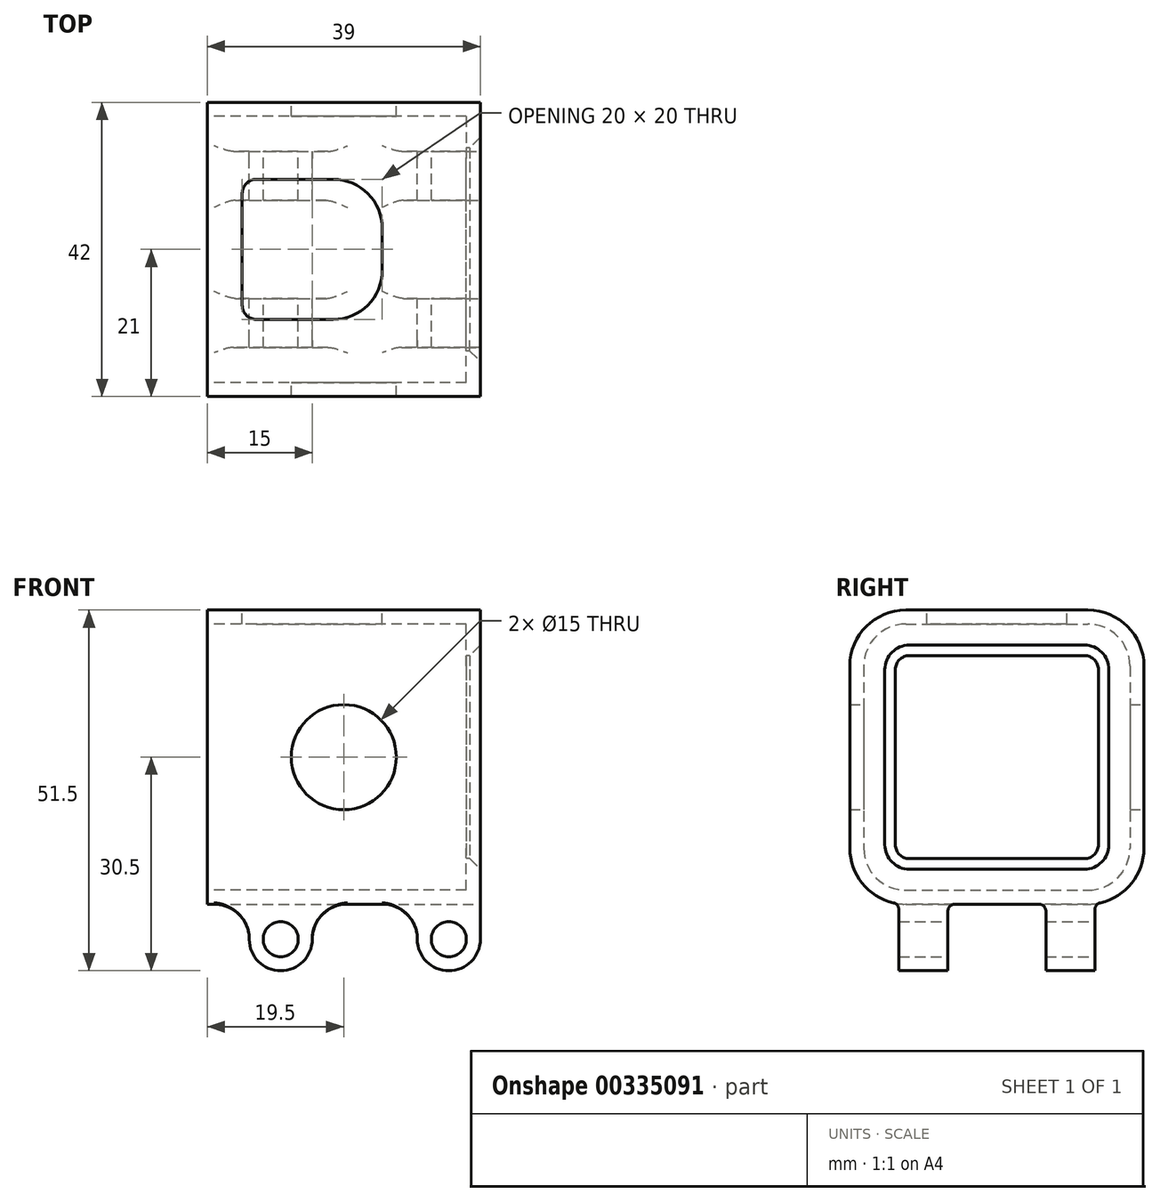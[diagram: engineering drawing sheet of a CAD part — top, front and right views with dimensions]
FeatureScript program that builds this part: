
annotation { "Feature Type Name" : "Feature", "Feature Type Description" : "" }
export const myFeature = defineFeature(function(context is Context, id is Id, definition is map)
    precondition{}
    {
        {
            var Q0;
            Q0=qCreatedBy(makeId("Right.planeOp"),FACE);
            var sketch = newSketch(context, id + "F0", { "sketchPlane" : qUnion([Q0])});
            skLineSegment(sketch, "E0.bottom", {"start": v(-13, 21) * mm, "end": v(13, 21) * mm});
            skLineSegment(sketch, "E0.top", {"start": v(-13, -21) * mm, "end": v(13, -21) * mm});
            skLineSegment(sketch, "E0.left", {"start": v(-21, 13) * mm, "end": v(-21, -13) * mm});
            skLineSegment(sketch, "E0.right", {"start": v(21, 13) * mm, "end": v(21, -13) * mm});
            skLineSegment(sketch, "E1.bottom", {"start": v(-13, 19) * mm, "end": v(13, 19) * mm});
            skLineSegment(sketch, "E1.top", {"start": v(-13, -19) * mm, "end": v(13, -19) * mm});
            skLineSegment(sketch, "E1.left", {"start": v(-19, 13) * mm, "end": v(-19, -13) * mm});
            skLineSegment(sketch, "E1.right", {"start": v(19, 13) * mm, "end": v(19, -13) * mm});
            skPoint(sketch, "E2.visualSharp", {"position": v(-19, 19) * mm});
            skArc(sketch, "E2.filletArc", {"start": v(-13, 19) * mm, "mid": v(-17.24, 17.24) * mm, "end": v(-19, 13) * mm});
            skPoint(sketch, "E3.visualSharp", {"position": v(19, 19) * mm});
            skArc(sketch, "E3.filletArc", {"start": v(19, 13) * mm, "mid": v(17.24, 17.24) * mm, "end": v(13, 19) * mm});
            skPoint(sketch, "E4.visualSharp", {"position": v(19, -19) * mm});
            skArc(sketch, "E4.filletArc", {"start": v(13, -19) * mm, "mid": v(17.24, -17.24) * mm, "end": v(19, -13) * mm});
            skPoint(sketch, "E5.visualSharp", {"position": v(-19, -19) * mm});
            skArc(sketch, "E5.filletArc", {"start": v(-19, -13) * mm, "mid": v(-17.24, -17.24) * mm, "end": v(-13, -19) * mm});
            skPoint(sketch, "E6.visualSharp", {"position": v(-21, -21) * mm});
            skArc(sketch, "E6.filletArc", {"start": v(-21, -13) * mm, "mid": v(-18.66, -18.66) * mm, "end": v(-13, -21) * mm});
            skPoint(sketch, "E7.visualSharp", {"position": v(21, -21) * mm});
            skArc(sketch, "E7.filletArc", {"start": v(13, -21) * mm, "mid": v(18.66, -18.66) * mm, "end": v(21, -13) * mm});
            skPoint(sketch, "E8.visualSharp", {"position": v(21, 21) * mm});
            skArc(sketch, "E8.filletArc", {"start": v(21, 13) * mm, "mid": v(18.66, 18.66) * mm, "end": v(13, 21) * mm});
            skPoint(sketch, "E9.visualSharp", {"position": v(-21, 21) * mm});
            skArc(sketch, "E9.filletArc", {"start": v(-13, 21) * mm, "mid": v(-18.66, 18.66) * mm, "end": v(-21, 13) * mm});
            skSolve(sketch);
        }
        {
            var Q0;
            Q0=qSketchRegion(id+"F0",true);
            extrude(context, id + "F1", {"entities" : qUnion([Q0]), "endBound" : BoundingType.SYMMETRIC, "depth" : 37 * mm});
        }
        {
            var Q0;
            Q0=makeQuery(id+"F1.opExtrude","CAP_FACE",FACE,{"disambiguationData":[OSD([sQuery(id+"F0.wireOp",EDGE,"E0.bottom"),sQuery(id+"F0.wireOp",EDGE,"E0.top"),sQuery(id+"F0.wireOp",EDGE,"E0.left"),sQuery(id+"F0.wireOp",EDGE,"E0.right"),sQuery(id+"F0.wireOp",EDGE,"E1.bottom"),sQuery(id+"F0.wireOp",EDGE,"E1.top"),sQuery(id+"F0.wireOp",EDGE,"E1.left"),sQuery(id+"F0.wireOp",EDGE,"E1.right"),sQuery(id+"F0.wireOp",EDGE,"E2.filletArc"),sQuery(id+"F0.wireOp",EDGE,"E3.filletArc"),sQuery(id+"F0.wireOp",EDGE,"E4.filletArc"),sQuery(id+"F0.wireOp",EDGE,"E5.filletArc"),sQuery(id+"F0.wireOp",EDGE,"E6.filletArc"),sQuery(id+"F0.wireOp",EDGE,"E7.filletArc"),sQuery(id+"F0.wireOp",EDGE,"E8.filletArc"),sQuery(id+"F0.wireOp",EDGE,"E9.filletArc")])],"isStart":false});
            var sketch = newSketch(context, id + "F2", { "sketchPlane" : qUnion([Q0])});
            skLineSegment(sketch, "E10.bottom", {"start": v(-12.5, 14.5) * mm, "end": v(12.5, 14.5) * mm});
            skLineSegment(sketch, "E10.top", {"start": v(-12.5, -14.5) * mm, "end": v(12.5, -14.5) * mm});
            skLineSegment(sketch, "E10.left", {"start": v(-14.5, 12.5) * mm, "end": v(-14.5, -12.5) * mm});
            skLineSegment(sketch, "E10.right", {"start": v(14.5, 12.5) * mm, "end": v(14.5, -12.5) * mm});
            skLineSegment(sketch, "E11.bottom", {"start": v(-13, 21) * mm, "end": v(13, 21) * mm});
            skLineSegment(sketch, "E11.top", {"start": v(-13, -21) * mm, "end": v(13, -21) * mm});
            skLineSegment(sketch, "E11.left", {"start": v(-21, 13) * mm, "end": v(-21, -13) * mm});
            skLineSegment(sketch, "E11.right", {"start": v(21, 13) * mm, "end": v(21, -13) * mm});
            skPoint(sketch, "E12.visualSharp", {"position": v(-21, 21) * mm});
            skArc(sketch, "E12.filletArc", {"start": v(-13, 21) * mm, "mid": v(-18.66, 18.66) * mm, "end": v(-21, 13) * mm});
            skPoint(sketch, "E13.visualSharp", {"position": v(-21, -21) * mm});
            skArc(sketch, "E13.filletArc", {"start": v(-21, -13) * mm, "mid": v(-18.66, -18.66) * mm, "end": v(-13, -21) * mm});
            skPoint(sketch, "E14.visualSharp", {"position": v(21, -21) * mm});
            skArc(sketch, "E14.filletArc", {"start": v(13, -21) * mm, "mid": v(18.66, -18.66) * mm, "end": v(21, -13) * mm});
            skPoint(sketch, "E15.visualSharp", {"position": v(21, 21) * mm});
            skArc(sketch, "E15.filletArc", {"start": v(21, 13) * mm, "mid": v(18.66, 18.66) * mm, "end": v(13, 21) * mm});
            skPoint(sketch, "E16.visualSharp", {"position": v(-14.5, 14.5) * mm});
            skArc(sketch, "E16.filletArc", {"start": v(-12.5, 14.5) * mm, "mid": v(-13.91, 13.91) * mm, "end": v(-14.5, 12.5) * mm});
            skPoint(sketch, "E17.visualSharp", {"position": v(-14.5, -14.5) * mm});
            skArc(sketch, "E17.filletArc", {"start": v(-14.5, -12.5) * mm, "mid": v(-13.91, -13.91) * mm, "end": v(-12.5, -14.5) * mm});
            skPoint(sketch, "E18.visualSharp", {"position": v(14.5, -14.5) * mm});
            skArc(sketch, "E18.filletArc", {"start": v(12.5, -14.5) * mm, "mid": v(13.91, -13.91) * mm, "end": v(14.5, -12.5) * mm});
            skPoint(sketch, "E19.visualSharp", {"position": v(14.5, 14.5) * mm});
            skArc(sketch, "E19.filletArc", {"start": v(14.5, 12.5) * mm, "mid": v(13.91, 13.91) * mm, "end": v(12.5, 14.5) * mm});
            skSolve(sketch);
        }
        {
            var Q0;
            Q0=qSketchRegion(id+"F2",true);
            extrude(context, id + "F3", {"entities" : qUnion([Q0]), "operationType" : NewBodyOperationType.ADD, "depth" : 2 * mm});
        }
        {
            var Q0;
            Q0=makeQuery(id+"F3.opExtrude","CAP_EDGE",EDGE,{"disambiguationData":[OSD([sQuery(id+"F2.wireOp",EDGE,"E10.bottom")])],"isStart":false});
            chamfer(context, id + "F4", {"entities" : qUnion([Q0]), "width" : 1.5 * mm, "tangentPropagation" : true});
        }
        {
            var Q0;
            Q0=makeQuery(id+"F3.boolean.opBoolean","MERGE",FACE,{"derivedFrom":[makeQuery(id+"F1.opExtrude","SWEPT_FACE",FACE,{"disambiguationData":[OSD([sQuery(id+"F0.wireOp",EDGE,"E0.bottom")])]}),makeQuery(id+"F3.opExtrude","SWEPT_FACE",FACE,{"disambiguationData":[OSD([sQuery(id+"F2.wireOp",EDGE,"E11.bottom")])]})]});
            var sketch = newSketch(context, id + "F5", { "sketchPlane" : qUnion([Q0])});
            skLineSegment(sketch, "E20.bottom", {"start": v(-11.5, 10) * mm, "end": v(-0.5, 10) * mm});
            skLineSegment(sketch, "E20.top", {"start": v(-11.5, -10) * mm, "end": v(-0.5, -10) * mm});
            skLineSegment(sketch, "E20.left", {"start": v(-13.5, 8) * mm, "end": v(-13.5, -8) * mm});
            skLineSegment(sketch, "E20.right", {"start": v(6.5, 3) * mm, "end": v(6.5, -3) * mm});
            skPoint(sketch, "E21.visualSharp", {"position": v(-13.5, 10) * mm});
            skArc(sketch, "E21.filletArc", {"start": v(-11.5, 10) * mm, "mid": v(-12.91, 9.41) * mm, "end": v(-13.5, 8) * mm});
            skPoint(sketch, "E22.visualSharp", {"position": v(-13.5, -10) * mm});
            skArc(sketch, "E22.filletArc", {"start": v(-13.5, -8) * mm, "mid": v(-12.91, -9.41) * mm, "end": v(-11.5, -10) * mm});
            skPoint(sketch, "E23.visualSharp", {"position": v(6.5, 10) * mm});
            skArc(sketch, "E23.filletArc", {"start": v(6.5, 3) * mm, "mid": v(4.45, 7.95) * mm, "end": v(-0.5, 10) * mm});
            skPoint(sketch, "E24.visualSharp", {"position": v(6.5, -10) * mm});
            skArc(sketch, "E24.filletArc", {"start": v(-0.5, -10) * mm, "mid": v(4.45, -7.95) * mm, "end": v(6.5, -3) * mm});
            skSolve(sketch);
        }
        {
            var Q0;
            Q0=qSketchRegion(id+"F5",true);
            extrude(context, id + "F6", {"entities" : qUnion([Q0]), "operationType" : NewBodyOperationType.REMOVE, "oppositeDirection" : true, "depth" : 5 * mm});
        }
        {
            var Q0;
            Q0=qCreatedBy(makeId("Front.planeOp"),FACE);
            var sketch = newSketch(context, id + "F7", { "sketchPlane" : qUnion([Q0])});
            skCircle(sketch, "E25", {"center": v(16, -26) * mm, "radius": 2.5 * mm});
            skCircle(sketch, "E26", {"center": v(-8, -26) * mm, "radius": 2.5 * mm});
            skLineSegment(sketch, "E27", {"start": v(-8, -26) * mm, "end": v(16, -26) * mm, "construction": true});
            skArc(sketch, "E28", {"start": v(11.5, -26) * mm, "mid": v(16, -30.5) * mm, "end": v(20.5, -26) * mm});
            skArc(sketch, "E29", {"start": v(-12.5, -26) * mm, "mid": v(-8, -30.5) * mm, "end": v(-3.5, -26) * mm});
            skLineSegment(sketch, "E30", {"start": v(20.5, -26) * mm, "end": v(20.5, -20) * mm});
            skLineSegment(sketch, "E31", {"start": v(11.5, -26) * mm, "end": v(11.5, -20) * mm});
            skLineSegment(sketch, "E32", {"start": v(-3.5, -26) * mm, "end": v(-3.5, -20) * mm});
            skLineSegment(sketch, "E33", {"start": v(-3.5, -20) * mm, "end": v(-12.5, -20) * mm});
            skLineSegment(sketch, "E34", {"start": v(-12.5, -20) * mm, "end": v(-12.5, -26) * mm});
            skLineSegment(sketch, "E35", {"start": v(-3.5, -20) * mm, "end": v(11.5, -20) * mm, "construction": true});
            skLineSegment(sketch, "E36", {"start": v(11.5, -20) * mm, "end": v(20.5, -20) * mm});
            skPoint(sketch, "E36.endSnap0", {"position": v(4, -20) * mm});
            skSolve(sketch);
        }
        {
            var Q0;
            Q0=qSketchRegion(id+"F7",true);
            extrude(context, id + "F8", {"entities" : qUnion([Q0]), "operationType" : NewBodyOperationType.ADD, "endBound" : BoundingType.SYMMETRIC, "depth" : 28 * mm});
        }
        {
            var Q0;
            Q0=makeQuery(id+"F8.boolean.opBoolean","INTERSECT",EDGE,{"derivedFrom":[makeQuery(id+"F3.boolean.opBoolean","MERGE",FACE,{"derivedFrom":[makeQuery(id+"F1.opExtrude","SWEPT_FACE",FACE,{"disambiguationData":[OSD([sQuery(id+"F0.wireOp",EDGE,"E0.top")])]}),makeQuery(id+"F3.opExtrude","SWEPT_FACE",FACE,{"disambiguationData":[OSD([sQuery(id+"F2.wireOp",EDGE,"E11.top")])]})]}),makeQuery(id+"F8.opExtrude","SWEPT_FACE",FACE,{"disambiguationData":[OSD([sQuery(id+"F7.wireOp",EDGE,"E34")])]})]});
            var Q1;
            Q1=makeQuery(id+"F8.boolean.opBoolean","INTERSECT",EDGE,{"derivedFrom":[makeQuery(id+"F3.boolean.opBoolean","MERGE",FACE,{"derivedFrom":[makeQuery(id+"F1.opExtrude","SWEPT_FACE",FACE,{"disambiguationData":[OSD([sQuery(id+"F0.wireOp",EDGE,"E0.top")])]}),makeQuery(id+"F3.opExtrude","SWEPT_FACE",FACE,{"disambiguationData":[OSD([sQuery(id+"F2.wireOp",EDGE,"E11.top")])]})]}),makeQuery(id+"F8.opExtrude","SWEPT_FACE",FACE,{"disambiguationData":[OSD([sQuery(id+"F7.wireOp",EDGE,"E32")])]})]});
            var Q2;
            Q2=makeQuery(id+"F8.boolean.opBoolean","INTERSECT",EDGE,{"derivedFrom":[makeQuery(id+"F3.boolean.opBoolean","MERGE",FACE,{"derivedFrom":[makeQuery(id+"F1.opExtrude","SWEPT_FACE",FACE,{"disambiguationData":[OSD([sQuery(id+"F0.wireOp",EDGE,"E0.top")])]}),makeQuery(id+"F3.opExtrude","SWEPT_FACE",FACE,{"disambiguationData":[OSD([sQuery(id+"F2.wireOp",EDGE,"E11.top")])]})]}),makeQuery(id+"F8.opExtrude","SWEPT_FACE",FACE,{"disambiguationData":[OSD([sQuery(id+"F7.wireOp",EDGE,"E31")])]})]});
            fillet(context, id + "F9", {"entities" : qUnion([Q0, Q1, Q2]), "radius" : 5 * mm, "tangentPropagation" : true, "allowEdgeOverflow" : false});
        }
        {
            var Q0;
            Q0=makeQuery(id+"F8.boolean.opBoolean","SPLIT",FACE,{"disambiguationData":[TD([makeQuery(id+"F8.opExtrude","SWEPT_FACE",FACE,{"disambiguationData":[OSD([sQuery(id+"F7.wireOp",EDGE,"E31")])]})])],"derivedFrom":makeQuery(id+"F3.boolean.opBoolean","MERGE",FACE,{"derivedFrom":[makeQuery(id+"F1.opExtrude","SWEPT_FACE",FACE,{"disambiguationData":[OSD([sQuery(id+"F0.wireOp",EDGE,"E0.top")])]}),makeQuery(id+"F3.opExtrude","SWEPT_FACE",FACE,{"disambiguationData":[OSD([sQuery(id+"F2.wireOp",EDGE,"E11.top")])]})]})});
            var sketch = newSketch(context, id + "F10", { "sketchPlane" : qUnion([Q0])});
            skLineSegment(sketch, "E37.bottom", {"start": v(-18.5, 7) * mm, "end": v(20.5, 7) * mm});
            skLineSegment(sketch, "E37.top", {"start": v(-18.5, -7) * mm, "end": v(20.5, -7) * mm});
            skLineSegment(sketch, "E37.left", {"start": v(-18.5, 7) * mm, "end": v(-18.5, -7) * mm});
            skLineSegment(sketch, "E37.right", {"start": v(20.5, 7) * mm, "end": v(20.5, -7) * mm});
            skSolve(sketch);
        }
        {
            var Q0;
            Q0=qSketchRegion(id+"F10",true);
            extrude(context, id + "F11", {"entities" : qUnion([Q0]), "operationType" : NewBodyOperationType.REMOVE, "depth" : 25 * mm});
        }
        {
            var Q0;
            {var subQ2=sQuery(id+"F10.wireOp",EDGE,"E37.bottom");Q0=makeQuery(id+"F11.boolean.opBoolean","COPY",EDGE,{"disambiguationData":[TD([makeQuery(id+"F8.opExtrude","SWEPT_FACE",FACE,{"disambiguationData":[OSD([sQuery(id+"F7.wireOp",EDGE,"E30")])]})])],"derivedFrom":makeQuery(id+"F11.opExtrude","CAP_EDGE",EDGE,{"disambiguationData":[OSD([subQ2])],"isStart":true})});}
            var Q1;
            {var subQ2=sQuery(id+"F10.wireOp",EDGE,"E37.top");Q1=makeQuery(id+"F11.boolean.opBoolean","COPY",EDGE,{"disambiguationData":[TD([makeQuery(id+"F8.opExtrude","SWEPT_FACE",FACE,{"disambiguationData":[OSD([sQuery(id+"F7.wireOp",EDGE,"E30")])]})])],"derivedFrom":makeQuery(id+"F11.opExtrude","CAP_EDGE",EDGE,{"disambiguationData":[OSD([subQ2])],"isStart":true})});}
            var Q2;
            {var subQ0=sQuery(id+"F2.wireOp",EDGE,"E11.top");var subQ1=sQuery(id+"F0.wireOp",EDGE,"E0.top");var subQ2=sQuery(id+"F10.wireOp",EDGE,"E37.bottom");Q2=makeQuery(id+"F11.boolean.opBoolean","COPY",EDGE,{"disambiguationData":[TD([makeQuery(id+"F9.opFillet","BLEND_FACE",FACE,{"disambiguationData":[OSD([subQ1,subQ0,sQuery(id+"F7.wireOp",EDGE,"E32")])]})])],"derivedFrom":makeQuery(id+"F11.opExtrude","CAP_EDGE",EDGE,{"disambiguationData":[OSD([subQ2])],"isStart":true})});}
            var Q3;
            {var subQ0=sQuery(id+"F2.wireOp",EDGE,"E11.top");var subQ1=sQuery(id+"F0.wireOp",EDGE,"E0.top");var subQ2=sQuery(id+"F10.wireOp",EDGE,"E37.top");Q3=makeQuery(id+"F11.boolean.opBoolean","COPY",EDGE,{"disambiguationData":[TD([makeQuery(id+"F9.opFillet","BLEND_FACE",FACE,{"disambiguationData":[OSD([subQ1,subQ0,sQuery(id+"F7.wireOp",EDGE,"E32")])]})])],"derivedFrom":makeQuery(id+"F11.opExtrude","CAP_EDGE",EDGE,{"disambiguationData":[OSD([subQ2])],"isStart":true})});}
            var Q4;
            Q4=makeQuery(id+"F8.boolean.opBoolean","INTERSECT",EDGE,{"derivedFrom":[makeQuery(id+"F3.boolean.opBoolean","MERGE",FACE,{"derivedFrom":[makeQuery(id+"F1.opExtrude","SWEPT_FACE",FACE,{"disambiguationData":[OSD([sQuery(id+"F0.wireOp",EDGE,"E6.filletArc")])]}),makeQuery(id+"F3.opExtrude","SWEPT_FACE",FACE,{"disambiguationData":[OSD([sQuery(id+"F2.wireOp",EDGE,"E13.filletArc")])]})]}),makeQuery(id+"F8.opExtrude","CAP_FACE",FACE,{"disambiguationData":[OSD([sQuery(id+"F7.wireOp",EDGE,"E25"),sQuery(id+"F7.wireOp",EDGE,"E28"),sQuery(id+"F7.wireOp",EDGE,"E30"),sQuery(id+"F7.wireOp",EDGE,"E31"),sQuery(id+"F7.wireOp",EDGE,"E36")])],"isStart":false})]});
            var Q5;
            Q5=makeQuery(id+"F8.boolean.opBoolean","INTERSECT",EDGE,{"derivedFrom":[makeQuery(id+"F3.boolean.opBoolean","MERGE",FACE,{"derivedFrom":[makeQuery(id+"F1.opExtrude","SWEPT_FACE",FACE,{"disambiguationData":[OSD([sQuery(id+"F0.wireOp",EDGE,"E6.filletArc")])]}),makeQuery(id+"F3.opExtrude","SWEPT_FACE",FACE,{"disambiguationData":[OSD([sQuery(id+"F2.wireOp",EDGE,"E13.filletArc")])]})]}),makeQuery(id+"F8.opExtrude","CAP_FACE",FACE,{"disambiguationData":[OSD([sQuery(id+"F7.wireOp",EDGE,"E26"),sQuery(id+"F7.wireOp",EDGE,"E29"),sQuery(id+"F7.wireOp",EDGE,"E32"),sQuery(id+"F7.wireOp",EDGE,"E33"),sQuery(id+"F7.wireOp",EDGE,"E34")])],"isStart":false})]});
            var Q6;
            Q6=makeQuery(id+"F8.boolean.opBoolean","INTERSECT",EDGE,{"derivedFrom":[makeQuery(id+"F3.boolean.opBoolean","MERGE",FACE,{"derivedFrom":[makeQuery(id+"F1.opExtrude","SWEPT_FACE",FACE,{"disambiguationData":[OSD([sQuery(id+"F0.wireOp",EDGE,"E7.filletArc")])]}),makeQuery(id+"F3.opExtrude","SWEPT_FACE",FACE,{"disambiguationData":[OSD([sQuery(id+"F2.wireOp",EDGE,"E14.filletArc")])]})]}),makeQuery(id+"F8.opExtrude","CAP_FACE",FACE,{"disambiguationData":[OSD([sQuery(id+"F7.wireOp",EDGE,"E26"),sQuery(id+"F7.wireOp",EDGE,"E29"),sQuery(id+"F7.wireOp",EDGE,"E32"),sQuery(id+"F7.wireOp",EDGE,"E33"),sQuery(id+"F7.wireOp",EDGE,"E34")])],"isStart":true})]});
            var Q7;
            Q7=makeQuery(id+"F8.boolean.opBoolean","INTERSECT",EDGE,{"derivedFrom":[makeQuery(id+"F3.boolean.opBoolean","MERGE",FACE,{"derivedFrom":[makeQuery(id+"F1.opExtrude","SWEPT_FACE",FACE,{"disambiguationData":[OSD([sQuery(id+"F0.wireOp",EDGE,"E7.filletArc")])]}),makeQuery(id+"F3.opExtrude","SWEPT_FACE",FACE,{"disambiguationData":[OSD([sQuery(id+"F2.wireOp",EDGE,"E14.filletArc")])]})]}),makeQuery(id+"F8.opExtrude","CAP_FACE",FACE,{"disambiguationData":[OSD([sQuery(id+"F7.wireOp",EDGE,"E25"),sQuery(id+"F7.wireOp",EDGE,"E28"),sQuery(id+"F7.wireOp",EDGE,"E30"),sQuery(id+"F7.wireOp",EDGE,"E31"),sQuery(id+"F7.wireOp",EDGE,"E36")])],"isStart":true})]});
            fillet(context, id + "F12", {"entities" : qUnion([Q0, Q1, Q2, Q3, Q4, Q5, Q6, Q7]), "radius" : 1 * mm, "tangentPropagation" : true, "allowEdgeOverflow" : false});
        }
        {
            var Q0;
            Q0=qCreatedBy(makeId("Front.planeOp"),FACE);
            var sketch = newSketch(context, id + "F13", { "sketchPlane" : qUnion([Q0])});
            skCircle(sketch, "E38", {"center": v(1, 0) * mm, "radius": 7.5 * mm});
            skSolve(sketch);
        }
        {
            var Q0;
            Q0=qSketchRegion(id+"F13",true);
            extrude(context, id + "F14", {"entities" : qUnion([Q0]), "operationType" : NewBodyOperationType.REMOVE, "endBound" : BoundingType.SYMMETRIC, "depth" : 45 * mm});
        }
    });
